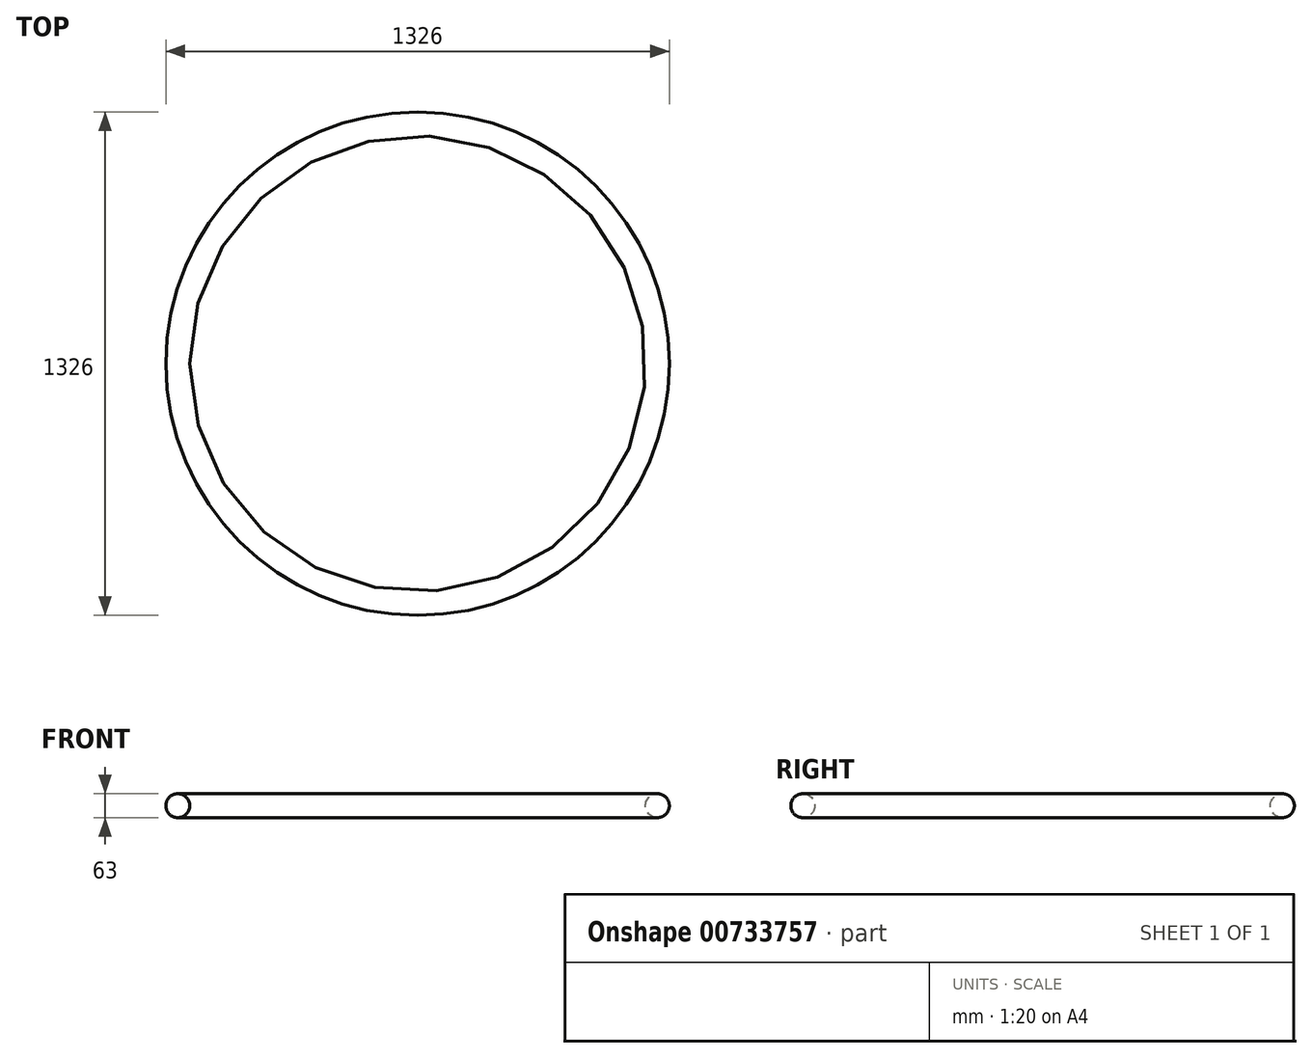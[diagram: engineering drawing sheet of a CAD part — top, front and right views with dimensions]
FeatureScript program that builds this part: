
annotation { "Feature Type Name" : "Feature", "Feature Type Description" : "" }
export const myFeature = defineFeature(function(context is Context, id is Id, definition is map)
    precondition{}
    {
        {
            var Q0;
            Q0=qCreatedBy(makeId("Front.planeOp"),FACE);
            var sketch = newSketch(context, id + "F0", { "sketchPlane" : qUnion([Q0])});
            skLineSegment(sketch, "E0", {"start": v(0, 0) * mm, "end": v(-631.5, 0) * mm});
            skCircle(sketch, "E1", {"center": v(-631.5, 0) * mm, "radius": 31.5 * mm});
            skLineSegment(sketch, "E2", {"start": v(0, 0) * mm, "end": v(0, 35.8) * mm});
            skSolve(sketch);
        }
        {
            var Q0;
            Q0=makeQuery(id+"F0.imprint","IMPRINT",FACE,{"disambiguationData":[TD([[makeQuery(id+"F0.imprint","IMPRINT",EDGE,{"derivedFrom":sQuery(id+"F0.wireOp",EDGE,"E1")}),1.0]])]});
            var Q1;
            Q1=sQuery(id+"F0.wireOp",EDGE,"E2");
            revolve(context, id + "F1", {"entities" : qUnion([Q0]), "axis" : qUnion([Q1]), "revolveType" : RevolveType.FULL});
        }
    });
